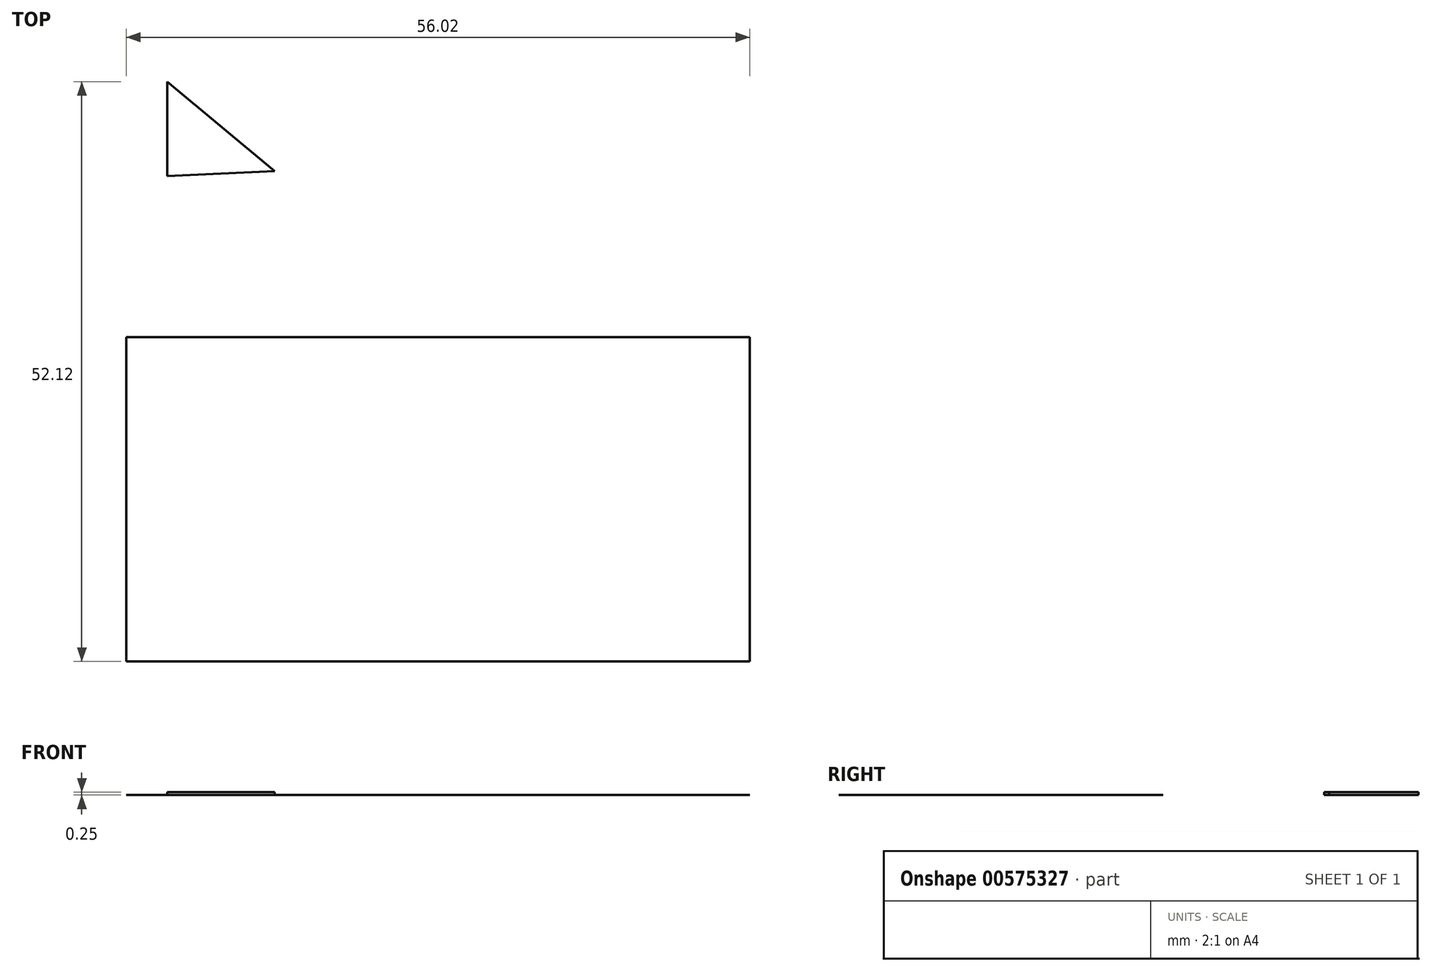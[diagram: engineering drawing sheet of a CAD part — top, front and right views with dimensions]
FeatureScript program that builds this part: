
annotation { "Feature Type Name" : "Feature", "Feature Type Description" : "" }
export const myFeature = defineFeature(function(context is Context, id is Id, definition is map)
    precondition{}
    {
        {
            var Q0;
            Q0=qCreatedBy(makeId("Top.planeOp"),FACE);
            var sketch = newSketch(context, id + "F0", { "sketchPlane" : qUnion([Q0])});
            skLineSegment(sketch, "E0.bottom", {"start": v(-28, 14.58) * mm, "end": v(28, 14.58) * mm});
            skLineSegment(sketch, "E0.top", {"start": v(-28, -14.58) * mm, "end": v(28, -14.58) * mm});
            skLineSegment(sketch, "E0.left", {"start": v(-28, 14.58) * mm, "end": v(-28, -14.58) * mm});
            skLineSegment(sketch, "E0.right", {"start": v(28, 14.58) * mm, "end": v(28, -14.58) * mm});
            skPoint(sketch, "E0.middle", {"position": v(0, 0) * mm});
            skSolve(sketch);
        }
        {
            var Q0;
            Q0=makeQuery(id+"F0.imprint","IMPRINT",FACE,{"disambiguationData":[TD([[makeQuery(id+"F0.imprint","IMPRINT",EDGE,{"derivedFrom":sQuery(id+"F0.wireOp",EDGE,"E0.bottom")}),-1.0]])]});
            extrude(context, id + "F1", {"entities" : qUnion([Q0]), "depth" : 0.03 * mm, "offsetDistance" : 25.4 * mm});
        }
        {
            var Q0;
            Q0=qCreatedBy(makeId("Top.planeOp"),FACE);
            var sketch = newSketch(context, id + "F2", { "sketchPlane" : qUnion([Q0])});
            skLineSegment(sketch, "E1", {"start": v(-24.34, 29.04) * mm, "end": v(-24.34, 37.54) * mm});
            skLineSegment(sketch, "E2", {"start": v(-24.34, 37.54) * mm, "end": v(-14.7, 29.5) * mm});
            skLineSegment(sketch, "E3", {"start": v(-14.7, 29.5) * mm, "end": v(-24.34, 29.04) * mm});
            skSolve(sketch);
        }
        {
            var Q0;
            Q0=makeQuery(id+"F2.imprint","IMPRINT",FACE,{"disambiguationData":[TD([[makeQuery(id+"F2.imprint","IMPRINT",EDGE,{"derivedFrom":sQuery(id+"F2.wireOp",EDGE,"E1")}),-1.0]])]});
            extrude(context, id + "F3", {"entities" : qUnion([Q0]), "depth" : 0.25 * mm, "offsetDistance" : 25.4 * mm});
        }
    });
